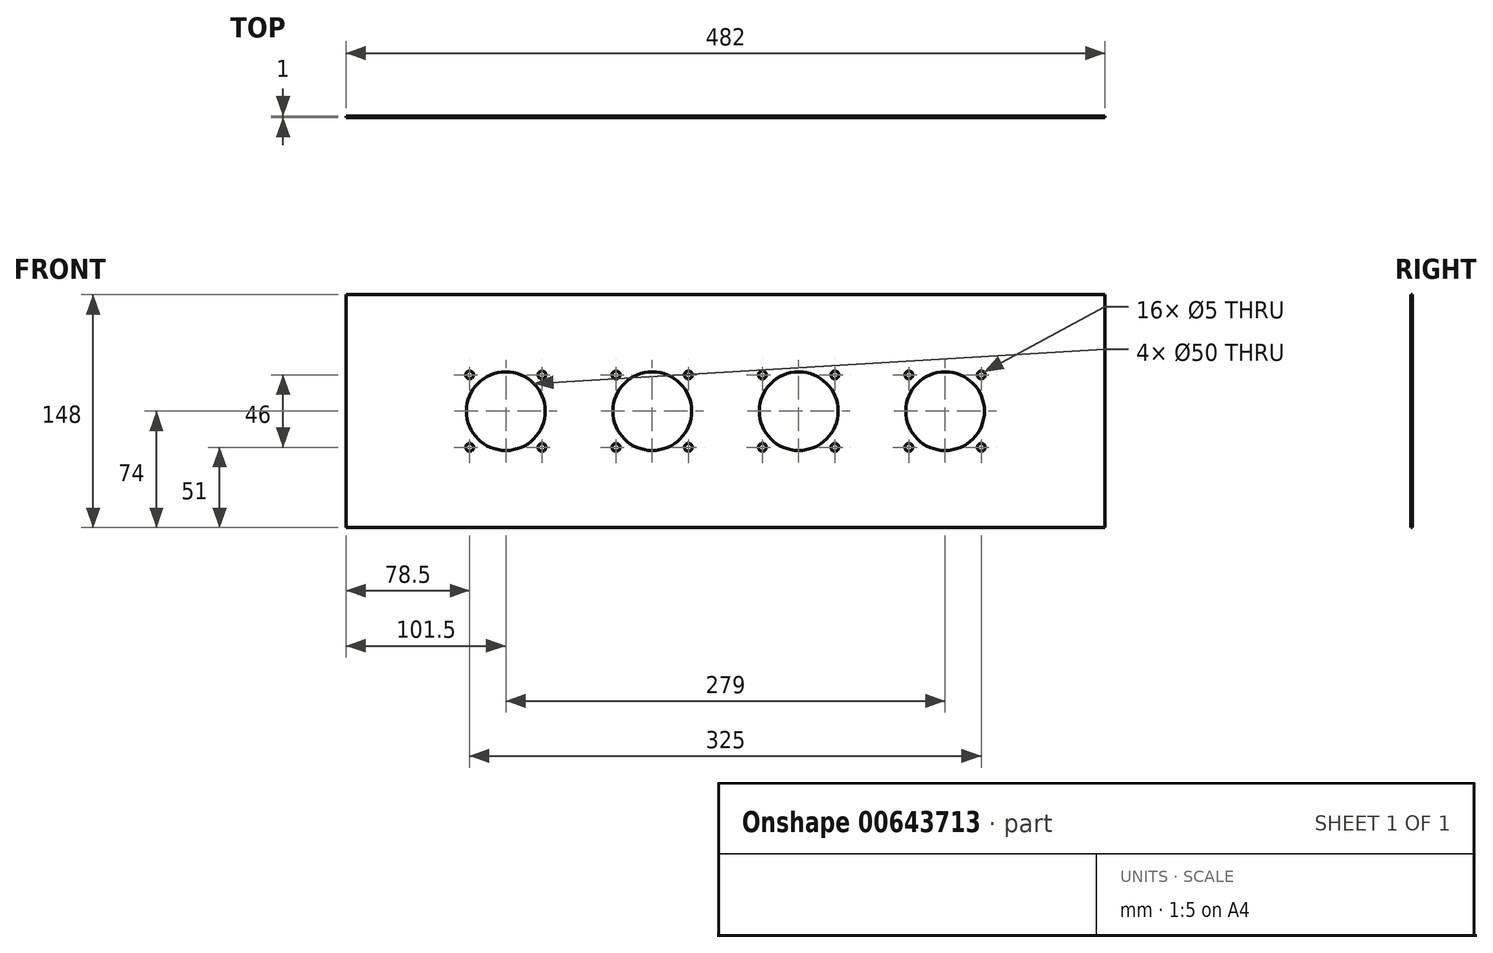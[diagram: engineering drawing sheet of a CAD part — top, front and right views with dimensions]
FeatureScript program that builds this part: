
annotation { "Feature Type Name" : "Feature", "Feature Type Description" : "" }
export const myFeature = defineFeature(function(context is Context, id is Id, definition is map)
    precondition{}
    {
        {
            var Q0;
            Q0=qCreatedBy(makeId("Front.planeOp"),FACE);
            var sketch = newSketch(context, id + "F0", { "sketchPlane" : qUnion([Q0])});
            skLineSegment(sketch, "E0.bottom", {"start": v(-241, -74) * mm, "end": v(241, -74) * mm});
            skLineSegment(sketch, "E0.top", {"start": v(-241, 74) * mm, "end": v(241, 74) * mm});
            skLineSegment(sketch, "E0.left", {"start": v(-241, -74) * mm, "end": v(-241, 74) * mm});
            skLineSegment(sketch, "E0.right", {"start": v(241, -74) * mm, "end": v(241, 74) * mm});
            skPoint(sketch, "E0.middle", {"position": v(0, 0) * mm});
            skPoint(sketch, "E1.middle", {"position": v(-139.5, 0) * mm});
            skCircle(sketch, "E2", {"center": v(-162.5, 23) * mm, "radius": 2.5 * mm});
            skCircle(sketch, "E3", {"center": v(-116.5, 23) * mm, "radius": 2.5 * mm});
            skCircle(sketch, "E4", {"center": v(-116.5, -23) * mm, "radius": 2.5 * mm});
            skCircle(sketch, "E5", {"center": v(-162.5, -23) * mm, "radius": 2.5 * mm});
            skCircle(sketch, "E6", {"center": v(-139.5, 0) * mm, "radius": 25 * mm});
            skPoint(sketch, "E7.middle", {"position": v(-46.5, 0) * mm});
            skCircle(sketch, "E8", {"center": v(-69.5, 23) * mm, "radius": 2.5 * mm});
            skCircle(sketch, "E9", {"center": v(-23.5, 23) * mm, "radius": 2.5 * mm});
            skCircle(sketch, "E10", {"center": v(-23.5, -23) * mm, "radius": 2.5 * mm});
            skCircle(sketch, "E11", {"center": v(-69.5, -23) * mm, "radius": 2.5 * mm});
            skCircle(sketch, "E12", {"center": v(-46.5, 0) * mm, "radius": 25 * mm});
            skPoint(sketch, "E13.middle", {"position": v(46.5, 0) * mm});
            skCircle(sketch, "E14", {"center": v(23.5, 23) * mm, "radius": 2.5 * mm});
            skCircle(sketch, "E15", {"center": v(69.5, 23) * mm, "radius": 2.5 * mm});
            skCircle(sketch, "E16", {"center": v(69.5, -23) * mm, "radius": 2.5 * mm});
            skCircle(sketch, "E17", {"center": v(23.5, -23) * mm, "radius": 2.5 * mm});
            skCircle(sketch, "E18", {"center": v(46.5, 0) * mm, "radius": 25 * mm});
            skPoint(sketch, "E19.middle", {"position": v(139.5, 0) * mm});
            skCircle(sketch, "E20", {"center": v(116.5, 23) * mm, "radius": 2.5 * mm});
            skCircle(sketch, "E21", {"center": v(162.5, 23) * mm, "radius": 2.5 * mm});
            skCircle(sketch, "E22", {"center": v(162.5, -23) * mm, "radius": 2.5 * mm});
            skCircle(sketch, "E23", {"center": v(116.5, -23) * mm, "radius": 2.5 * mm});
            skCircle(sketch, "E24", {"center": v(139.5, 0) * mm, "radius": 25 * mm});
            skSolve(sketch);
        }
        {
            var Q0;
            Q0 = qSketchRegion(id + "F0", true);
            var Q1;
            Q1=makeQuery(id+"F0.imprint","IMPRINT",FACE,{"disambiguationData":[TD([[makeQuery(id+"F0.imprint","IMPRINT",EDGE,{"derivedFrom":sQuery(id+"F0.wireOp",EDGE,"E0.bottom")}),1.0]])]});
            extrude(context, id + "F1", {"entities" : qUnion([Q0, Q1]), "endBound" : BoundingType.SYMMETRIC, "depth" : 1 * mm, "offsetDistance" : 25 * mm});
        }
    });
